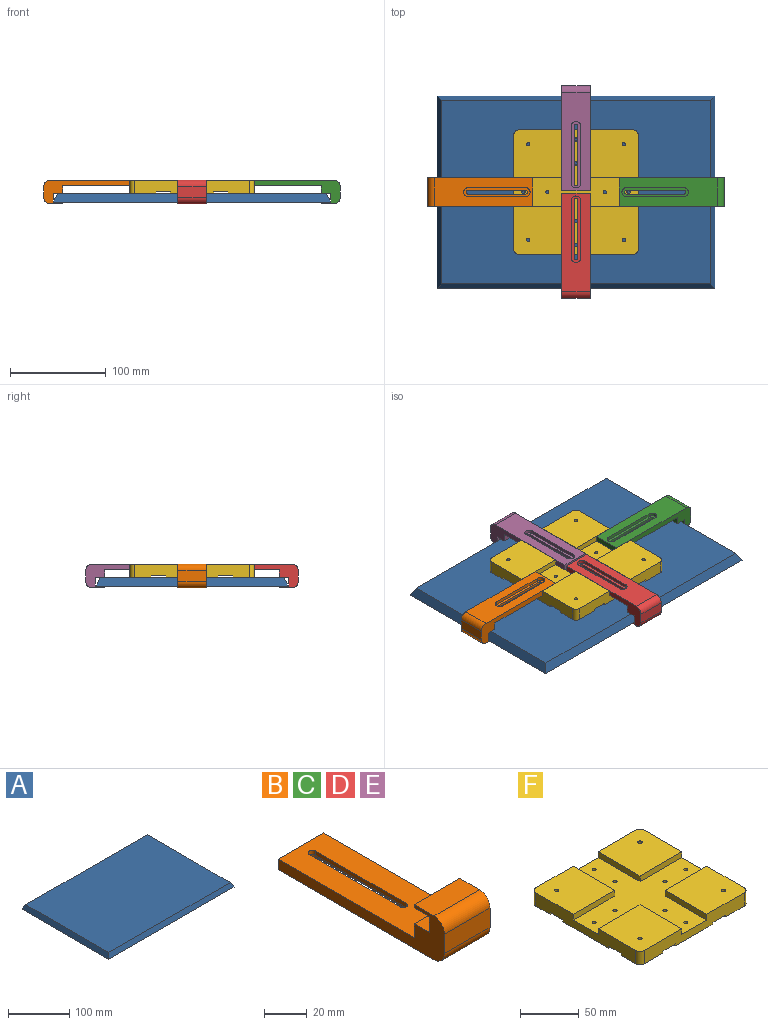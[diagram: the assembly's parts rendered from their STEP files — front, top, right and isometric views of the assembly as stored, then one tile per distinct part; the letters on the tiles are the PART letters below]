
ASSEMBLY  parts=6 mates=5
PART A: 6 faces, bbox 290x201x9.1 mm
  f0: plane 280.98x191.98mm, normal (0,0,1), area 53942.5mm2, adj f2,f3,f4,f5
  f1: plane 290x201mm, normal (0,0,-1), area 58290mm2, adj f2,f3,f4,f5
  f2: plane 201x9.1mm, normal (-0.9,0,0.44), area 1995.6mm2, adj f0,f1,f3,f4
  f3: plane 290x9.1mm, normal (0,0.9,0.44), area 2899.5mm2, adj f0,f1,f2,f5
  f4: plane 290x9.1mm, normal (0,-0.9,0.44), area 2899.5mm2, adj f0,f1,f2,f5
  f5: plane 201x9.1mm, normal (0.9,0,0.44), area 1995.6mm2, adj f0,f1,f3,f4
PART B: 23 faces, bbox 30x110x25 mm
  f0: plane 103x30mm, normal (0,0,-1), area 2449.1mm2, adj f6,f8,f9,f16,f17,f18,f19,f22
  f1: cylinder r=2mm len=4mm, axis (0,0,-1), area 15.7mm2, adj f2,f4,f7,f20
  f2: plane 60x2.5mm, normal (-1,0,0), area 150mm2, adj f1,f3,f7,f20
  f3: cylinder r=2mm len=4mm, axis (0,0,-1), area 15.7mm2, adj f2,f4,f7,f20
  f4: plane 60x2.5mm, normal (1,0,0), area 150mm2, adj f1,f3,f7,f20
  f5: plane 30x8mm, normal (0,1,0), area 240mm2, adj f6,f7,f9,f13
  f6: plane 110x25mm, normal (1,0,0), area 928mm2, adj f0,f5,f7,f8,f10,f11,f12,f13
  f7: plane 90x30mm, normal (0,0,1), area 2447.4mm2, adj f1,f2,f3,f4,f5,f6,f8,f9
  f8: plane 30x6mm, normal (0,1,0), area 180mm2, adj f0,f6,f7,f9
  f9: plane 110x25mm, normal (-1,0,0), area 928mm2, adj f0,f5,f7,f8,f10,f11,f12,f13
  f10: plane 30x11mm, normal (0,-1,0), area 330mm2, adj f6,f9,f21,f22
  f11: plane 30x1.9mm, normal (0,1,0), area 57mm2, adj f6,f9,f12,f14
  f12: plane 30x13mm, normal (0,0,1), area 390mm2, adj f6,f9,f11,f21
  f13: plane 30x10mm, normal (0,0,1), area 300mm2, adj f5,f6,f9,f15
  f14: plane 30x10mm, normal (0,0,-1), area 300mm2, adj f6,f9,f11,f15
  f15: plane 30x9.1mm, normal (0,1,0), area 273mm2, adj f6,f9,f13,f14
  f16: plane 60x3.5mm, normal (1,0,0), area 210mm2, adj f0,f17,f19,f20
  f17: cylinder r=4.75mm len=9.5mm, axis (0,0,-1), area 52.2mm2, adj f0,f16,f18,f20
  f18: plane 60x3.5mm, normal (-1,0,0), area 210mm2, adj f0,f17,f19,f20
  f19: cylinder r=4.75mm len=9.5mm, axis (0,0,-1), area 52.2mm2, adj f0,f16,f18,f20
  f20: plane 69.5x9.5mm, normal (0,0,-1), area 388.3mm2, adj f1,f2,f3,f4,f16,f17,f18,f19
  f21: cylinder r=7mm len=30mm, axis (-1,0,0), area 329.9mm2, adj f6,f9,f10,f12
  f22: cylinder r=7mm len=30mm, axis (1,0,0), area 329.9mm2, adj f0,f6,f9,f10
PART C: same geometry as B
PART D: same geometry as B
PART E: same geometry as B
PART F: 67 faces, bbox 130x130x14 mm
  f0: plane 120x14mm, normal (0,-1,0), area 1440mm2, adj f11,f12,f19,f20,f26,f31,f32,f36
  f1: plane 120x14mm, normal (1,0,0), area 1440mm2, adj f10,f11,f13,f19,f27,f33,f34,f36
  f2: cylinder r=1.75mm len=6mm, axis (0,0,1), area 66mm2, adj f36,f61
  f3: cylinder r=1.75mm len=6mm, axis (0,0,1), area 66mm2, adj f36,f61
  f4: cylinder r=1.75mm len=6mm, axis (0,0,1), area 66mm2, adj f36,f61
  f5: cylinder r=1.75mm len=6mm, axis (0,0,1), area 66mm2, adj f36,f61
  f6: plane 120x14mm, normal (0,1,0), area 1440mm2, adj f8,f9,f13,f18,f27,f28,f35,f36
  f7: plane 55x27.5mm, normal (0,0,-1), area 1502.9mm2, adj f16,f21,f41,f42,f43
  f8: plane 27.5x22.5mm, normal (0,0,-1), area 603.8mm2, adj f6,f21,f25,f44,f45,f63
  f9: plane 45x22.5mm, normal (0,0,-1), area 1002.9mm2, adj f6,f15,f46,f47,f48
  f10: plane 55x27.5mm, normal (0,0,-1), area 1502.9mm2, adj f1,f17,f51,f52,f53
  f11: plane 27.5x22.5mm, normal (0,0,-1), area 603.8mm2, adj f0,f1,f23,f54,f55,f65
  f12: plane 45x22.5mm, normal (0,0,-1), area 1002.9mm2, adj f0,f14,f56,f57,f58
  f13: plane 27.5x22.5mm, normal (0,0,-1), area 603.8mm2, adj f1,f6,f24,f49,f50,f64
  f14: cylinder r=1.75mm len=8mm, axis (0,0,1), area 88mm2, adj f12,f36
  f15: cylinder r=1.75mm len=8mm, axis (0,0,1), area 88mm2, adj f9,f36
  f16: cylinder r=1.75mm len=8mm, axis (0,0,1), area 88mm2, adj f7,f36
  f17: cylinder r=1.75mm len=8mm, axis (0,0,1), area 88mm2, adj f10,f36
  f18: plane 50x50mm, normal (0,0,1), area 2485mm2, adj f6,f21,f25,f28,f29,f63
  f19: plane 50x50mm, normal (0,0,1), area 2485mm2, adj f0,f1,f23,f32,f33,f65
  f20: plane 50x50mm, normal (0,0,1), area 2485mm2, adj f0,f21,f22,f30,f31,f66
  f21: plane 120x14mm, normal (-1,0,0), area 1440mm2, adj f7,f8,f18,f20,f26,f29,f30,f36
  f22: cylinder r=1.75mm len=14mm, axis (0,0,1), area 153.9mm2, adj f20,f26
  f23: cylinder r=1.75mm len=14mm, axis (0,0,1), area 153.9mm2, adj f11,f19
  f24: cylinder r=1.75mm len=14mm, axis (0,0,1), area 153.9mm2, adj f13,f27
  f25: cylinder r=1.75mm len=14mm, axis (0,0,1), area 153.9mm2, adj f8,f18
  f26: plane 27.5x22.5mm, normal (0,0,-1), area 603.8mm2, adj f0,f21,f22,f40,f59,f66
  f27: plane 50x50mm, normal (0,0,1), area 2485mm2, adj f1,f6,f24,f34,f35,f64
  f28: plane 50x6mm, normal (1,0,0), area 300mm2, adj f6,f18,f29,f36
  f29: plane 50x6mm, normal (0,-1,0), area 300mm2, adj f18,f21,f28,f36
  f30: plane 50x6mm, normal (0,1,0), area 300mm2, adj f20,f21,f31,f36
  f31: plane 50x6mm, normal (1,0,0), area 300mm2, adj f0,f20,f30,f36
  f32: plane 50x6mm, normal (-1,0,0), area 300mm2, adj f0,f19,f33,f36
  f33: plane 50x6mm, normal (0,1,0), area 300mm2, adj f1,f19,f32,f36
  f34: plane 50x6mm, normal (0,-1,0), area 300mm2, adj f1,f27,f35,f36
  f35: plane 50x6mm, normal (-1,0,0), area 300mm2, adj f6,f27,f34,f36
  f36: plane 130x130mm, normal (0,0,1), area 6823mm2, adj f0,f1,f2,f3,f4,f5,f6,f14
  f37: plane 55x2mm, normal (-1,0,0), area 110mm2, adj f38,f60,f61,f62
  f38: plane 45x2mm, normal (0,-1,0), area 90mm2, adj f37,f39,f61,f62
  f39: plane 55x2mm, normal (1,0,0), area 110mm2, adj f38,f60,f61,f62
  f40: plane 27.5x2mm, normal (0,1,0), area 55mm2, adj f21,f26,f59,f61
  f41: plane 27.5x2mm, normal (0,-1,0), area 55mm2, adj f7,f21,f42,f61
  f42: plane 55x2mm, normal (1,0,0), area 110mm2, adj f7,f41,f43,f61
  f43: plane 27.5x2mm, normal (0,1,0), area 55mm2, adj f7,f21,f42,f61
  f44: plane 27.5x2mm, normal (0,-1,0), area 55mm2, adj f8,f21,f45,f61
  f45: plane 22.5x2mm, normal (1,0,0), area 45mm2, adj f6,f8,f44,f61
  f46: plane 22.5x2mm, normal (-1,0,0), area 45mm2, adj f6,f9,f47,f61
  f47: plane 45x2mm, normal (0,-1,0), area 90mm2, adj f9,f46,f48,f61
  f48: plane 22.5x2mm, normal (1,0,0), area 45mm2, adj f6,f9,f47,f61
  f49: plane 22.5x2mm, normal (-1,0,0), area 45mm2, adj f6,f13,f50,f61
  f50: plane 27.5x2mm, normal (0,-1,0), area 55mm2, adj f1,f13,f49,f61
  f51: plane 27.5x2mm, normal (0,1,0), area 55mm2, adj f1,f10,f52,f61
  f52: plane 55x2mm, normal (-1,0,0), area 110mm2, adj f10,f51,f53,f61
  f53: plane 27.5x2mm, normal (0,-1,0), area 55mm2, adj f1,f10,f52,f61
  f54: plane 27.5x2mm, normal (0,1,0), area 55mm2, adj f1,f11,f55,f61
  f55: plane 22.5x2mm, normal (-1,0,0), area 45mm2, adj f0,f11,f54,f61
  f56: plane 22.5x2mm, normal (1,0,0), area 45mm2, adj f0,f12,f57,f61
  f57: plane 45x2mm, normal (0,1,0), area 90mm2, adj f12,f56,f58,f61
  f58: plane 22.5x2mm, normal (-1,0,0), area 45mm2, adj f0,f12,f57,f61
  f59: plane 22.5x2mm, normal (1,0,0), area 45mm2, adj f0,f26,f40,f61
  f60: plane 45x2mm, normal (0,1,0), area 90mm2, adj f37,f39,f61,f62
  f61: plane 130x130mm, normal (0,0,-1), area 6861.5mm2, adj f0,f1,f2,f3,f4,f5,f6,f21
  f62: plane 55x45mm, normal (0,0,-1), area 2475mm2, adj f37,f38,f39,f60
  f63: cylinder r=5mm len=14mm, axis (0,0,-1), area 110mm2, adj f6,f8,f18,f21
  f64: cylinder r=5mm len=14mm, axis (0,0,1), area 110mm2, adj f1,f6,f13,f27
  f65: cylinder r=5mm len=14mm, axis (0,0,1), area 110mm2, adj f0,f1,f11,f19
  f66: cylinder r=5mm len=14mm, axis (0,0,-1), area 110mm2, adj f0,f20,f21,f26
PLACE A t=(57.66,-53.37,-17.1)mm
PLACE B rot(axis=(-0.71,-0.71,0),180deg) t=(-30,0,0)mm
PLACE C rot(axis=(-0.71,0.71,0),180deg) t=(30,0,0)mm
PLACE D rot(axis=(0,1,0),180deg) t=(0,13.95,0)mm
PLACE E rot(axis=(-1,0,0),180deg) t=(0,-13.68,0)mm
PLACE F t=(0,0,6)mm
MATE slider F.f6 <-> E.f8  axis (0,1,0) through (-15,65,0)mm
MATE slider F.f0 <-> D.f8  axis (0,-1,0) through (-15,-65,0)mm
MATE fastened F.f62 <-> A.f0  axis (0,0,-1) through (0,0,-8)mm
MATE slider F.f1 <-> C.f8  axis (-1,0,0) through (65,-15,0)mm
MATE slider B.f8 <-> F.f21  axis (-1,0,0) through (-45,15,0)mm
